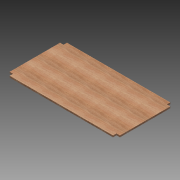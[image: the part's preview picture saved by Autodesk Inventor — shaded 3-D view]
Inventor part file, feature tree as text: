
AUTODESK INVENTOR PART (.ipt)
format: ipt  version: 2013 (Build 170138000, 138)  size: 104,960 bytes
history: native  units: in
note: dims shown in document units (in); Inventor stores cm internally (conversion verified against a paired STEP export)
features: extrude x1, sketch x1
ambient origin geometry x8: Origin, YZ Plane, XZ Plane, XY Plane, X Axis, Y Axis, Z Axis, Center Point
bodies: Solid1 (feature_tree)
feature tree (2):
  extrude  "Extrusion1"  Depth=1.625in
  sketch  "Sketch1"  dims[d2=1.625in d3=1.625in d4=1.625in d5=1.625in d6=1.625in d7=1.625in d8=1.625in d9=1.625in d10=90.0deg d11=90.0deg d12=90.0deg d13=90.0deg d14=90.0deg d15=90.0deg d16=90.0deg d17=90.0deg d18=0.75in d19=0.0in d20=27.0in]
